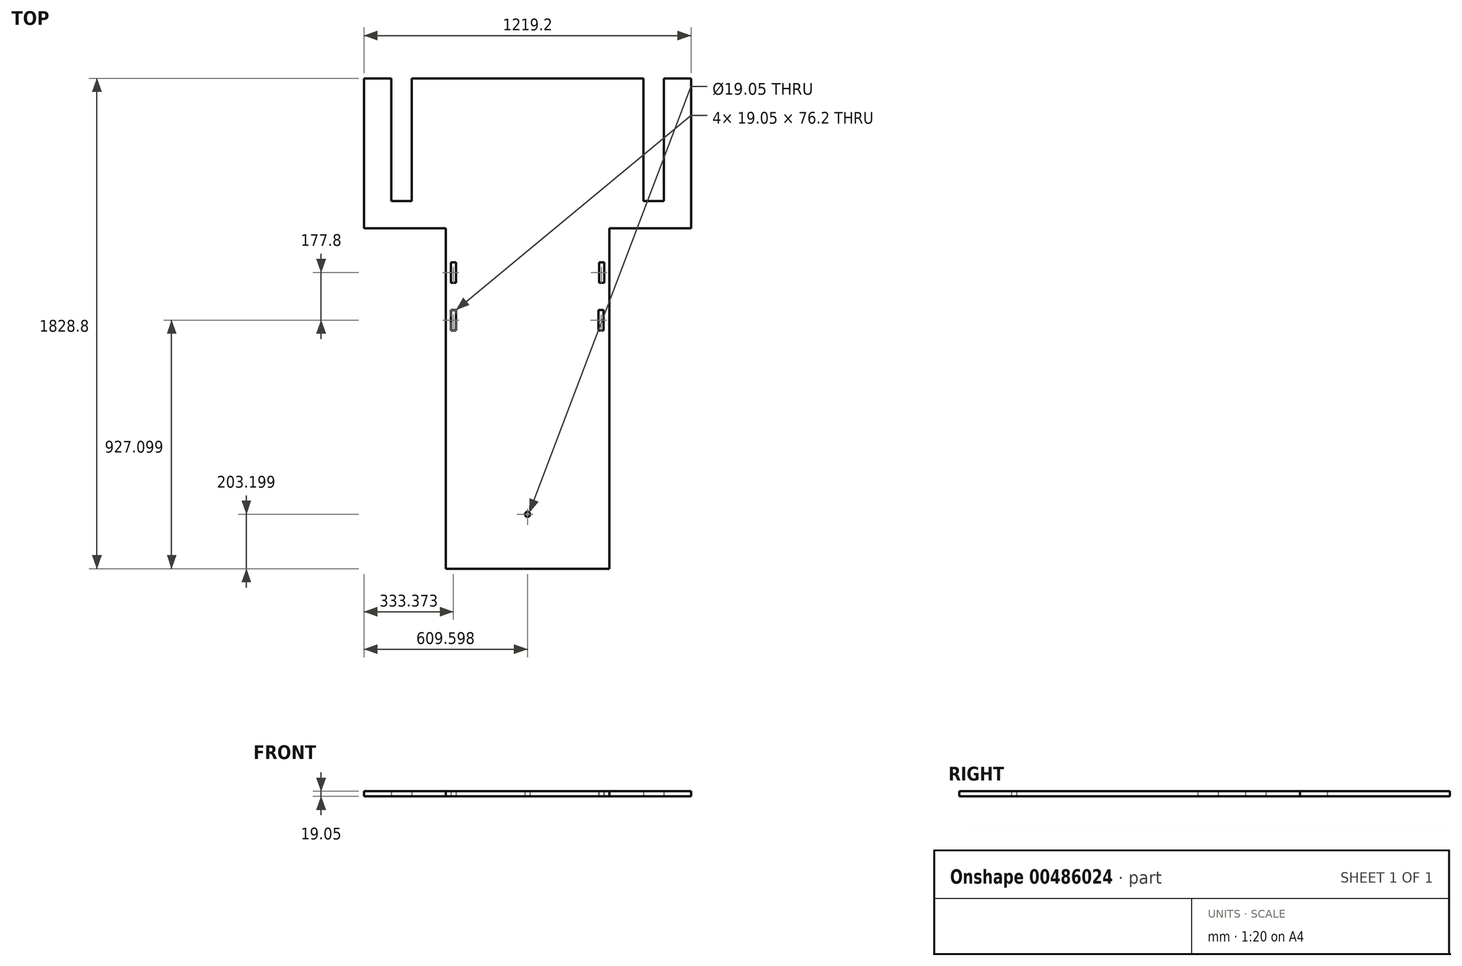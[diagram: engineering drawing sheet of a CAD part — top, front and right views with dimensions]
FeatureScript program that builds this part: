
annotation { "Feature Type Name" : "Feature", "Feature Type Description" : "" }
export const myFeature = defineFeature(function(context is Context, id is Id, definition is map)
    precondition{}
    {
        {
            var Q0;
            Q0=qCreatedBy(makeId("Top.planeOp"),FACE);
            var sketch = newSketch(context, id + "F0", { "sketchPlane" : qUnion([Q0])});
            skLineSegment(sketch, "E0.bottom", {"start": v(-287.56, -201.46) * mm, "end": v(322.04, -201.46) * mm});
            skLineSegment(sketch, "E0.left", {"start": v(-287.56, -201.46) * mm, "end": v(-287.56, 204.94) * mm});
            skLineSegment(sketch, "E0.right", {"start": v(322.04, -201.46) * mm, "end": v(322.04, 204.94) * mm});
            skLineSegment(sketch, "E1", {"start": v(-287.56, 1068.54) * mm, "end": v(-592.36, 1068.54) * mm});
            skLineSegment(sketch, "E2", {"start": v(322.04, 1068.54) * mm, "end": v(626.84, 1068.54) * mm});
            skLineSegment(sketch, "E3", {"start": v(-490.76, 1170.14) * mm, "end": v(-490.76, 1627.34) * mm});
            skLineSegment(sketch, "E4", {"start": v(-490.76, 1170.14) * mm, "end": v(-414.56, 1170.14) * mm});
            skLineSegment(sketch, "E5", {"start": v(-414.56, 1170.14) * mm, "end": v(-414.56, 1627.34) * mm});
            skLineSegment(sketch, "E6", {"start": v(-490.76, 1627.34) * mm, "end": v(-592.36, 1627.34) * mm});
            skLineSegment(sketch, "E7", {"start": v(-592.36, 1627.34) * mm, "end": v(-592.36, 1068.54) * mm});
            skLineSegment(sketch, "E8", {"start": v(322.04, -201.46) * mm, "end": v(17.24, -201.46) * mm});
            skCircle(sketch, "E9", {"center": v(17.24, 1.74) * mm, "radius": 9.52 * mm});
            skLineSegment(sketch, "E10", {"start": v(-287.56, 1068.54) * mm, "end": v(-287.56, 941.54) * mm});
            skLineSegment(sketch, "E11", {"start": v(-287.56, 941.54) * mm, "end": v(-287.56, 865.34) * mm});
            skLineSegment(sketch, "E12", {"start": v(-287.56, 560.54) * mm, "end": v(-287.56, 687.54) * mm});
            skLineSegment(sketch, "E13", {"start": v(-287.56, 687.54) * mm, "end": v(-287.56, 763.74) * mm});
            skLineSegment(sketch, "E14", {"start": v(-268.51, 941.54) * mm, "end": v(-268.51, 865.34) * mm});
            skLineSegment(sketch, "E15", {"start": v(-268.51, 865.34) * mm, "end": v(-249.46, 865.34) * mm});
            skLineSegment(sketch, "E16", {"start": v(-249.46, 865.34) * mm, "end": v(-249.46, 941.54) * mm});
            skLineSegment(sketch, "E17", {"start": v(-249.46, 941.54) * mm, "end": v(-268.51, 941.54) * mm});
            skLineSegment(sketch, "E18", {"start": v(-268.51, 687.54) * mm, "end": v(-268.51, 763.74) * mm});
            skLineSegment(sketch, "E19", {"start": v(-268.51, 763.74) * mm, "end": v(-249.46, 763.74) * mm});
            skLineSegment(sketch, "E20", {"start": v(-249.46, 763.74) * mm, "end": v(-249.46, 687.54) * mm});
            skLineSegment(sketch, "E21", {"start": v(-249.46, 687.54) * mm, "end": v(-268.51, 687.54) * mm});
            skLineSegment(sketch, "E22", {"start": v(-287.56, 1068.54) * mm, "end": v(-287.56, 204.94) * mm});
            skLineSegment(sketch, "E23", {"start": v(322.04, 1068.54) * mm, "end": v(322.04, 941.54) * mm});
            skLineSegment(sketch, "E24", {"start": v(322.04, 941.54) * mm, "end": v(322.04, 865.34) * mm});
            skLineSegment(sketch, "E25", {"start": v(319.96, 559.77) * mm, "end": v(319.96, 686.77) * mm});
            skLineSegment(sketch, "E26", {"start": v(319.96, 686.77) * mm, "end": v(319.96, 762.97) * mm});
            skLineSegment(sketch, "E27", {"start": v(302.99, 941.54) * mm, "end": v(302.99, 865.34) * mm});
            skLineSegment(sketch, "E28", {"start": v(302.99, 865.34) * mm, "end": v(283.94, 865.34) * mm});
            skLineSegment(sketch, "E29", {"start": v(283.94, 865.34) * mm, "end": v(283.94, 941.54) * mm});
            skLineSegment(sketch, "E30", {"start": v(302.99, 941.54) * mm, "end": v(283.94, 941.54) * mm});
            skLineSegment(sketch, "E31", {"start": v(300.9, 762.97) * mm, "end": v(300.9, 686.77) * mm});
            skLineSegment(sketch, "E32", {"start": v(300.9, 686.77) * mm, "end": v(281.86, 686.77) * mm});
            skLineSegment(sketch, "E33", {"start": v(281.86, 686.77) * mm, "end": v(281.86, 762.97) * mm});
            skLineSegment(sketch, "E34", {"start": v(281.86, 762.97) * mm, "end": v(300.9, 762.97) * mm});
            skLineSegment(sketch, "E35", {"start": v(322.04, 204.94) * mm, "end": v(322.04, 1068.54) * mm});
            skLineSegment(sketch, "E36", {"start": v(626.84, 1068.54) * mm, "end": v(626.84, 1627.34) * mm});
            skLineSegment(sketch, "E37", {"start": v(525.24, 1627.34) * mm, "end": v(525.24, 1170.14) * mm});
            skLineSegment(sketch, "E38", {"start": v(525.24, 1170.14) * mm, "end": v(449.04, 1170.14) * mm});
            skLineSegment(sketch, "E39", {"start": v(449.04, 1170.14) * mm, "end": v(449.04, 1627.34) * mm});
            skLineSegment(sketch, "E40", {"start": v(525.24, 1627.34) * mm, "end": v(626.84, 1627.34) * mm});
            skLineSegment(sketch, "E41", {"start": v(449.04, 1627.34) * mm, "end": v(-414.56, 1627.34) * mm});
            skSolve(sketch);
        }
        {
            var Q0;
            Q0 = qSketchRegion(id + "F0", true);
            extrude(context, id + "F1", {"entities" : qUnion([Q0]), "depth" : 19.05 * mm, "offsetDistance" : 25.4 * mm});
        }
    });
